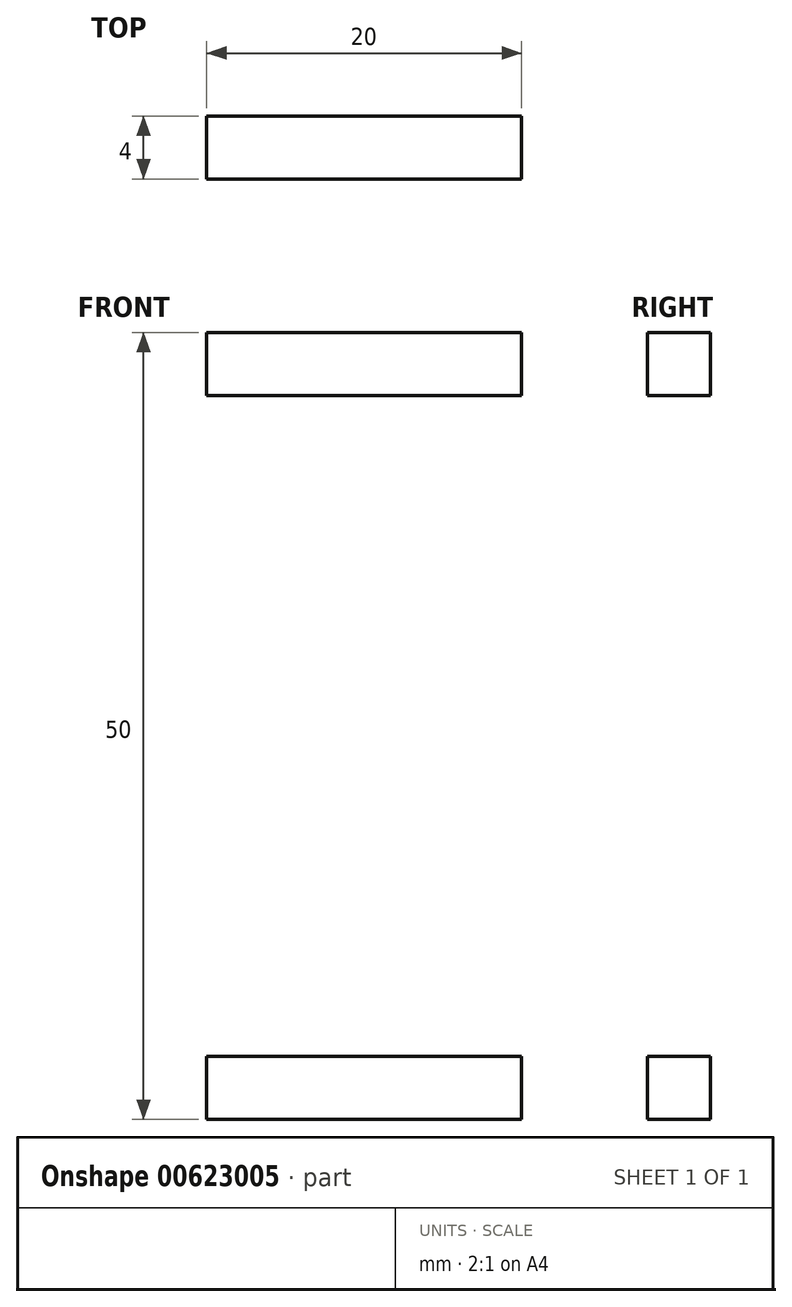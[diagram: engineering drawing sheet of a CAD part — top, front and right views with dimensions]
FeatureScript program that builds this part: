
annotation { "Feature Type Name" : "Feature", "Feature Type Description" : "" }
export const myFeature = defineFeature(function(context is Context, id is Id, definition is map)
    precondition{}
    {
        {
            var Q0;
            Q0=qCreatedBy(makeId("Front.planeOp"),FACE);
            var sketch = newSketch(context, id + "F0", { "sketchPlane" : qUnion([Q0])});
            skLineSegment(sketch, "E0.bottom", {"start": v(0, 0) * mm, "end": v(-300, 0) * mm});
            skLineSegment(sketch, "E0.top", {"start": v(0, 50) * mm, "end": v(-300, 50) * mm});
            skLineSegment(sketch, "E0.left", {"start": v(0, 0) * mm, "end": v(0, 50) * mm});
            skLineSegment(sketch, "E0.right", {"start": v(-300, 0) * mm, "end": v(-300, 50) * mm});
            skLineSegment(sketch, "E1.bottom", {"start": v(-300, 0) * mm, "end": v(-280, 0) * mm});
            skLineSegment(sketch, "E1.top", {"start": v(-300, 4) * mm, "end": v(-280, 4) * mm});
            skLineSegment(sketch, "E1.left", {"start": v(-300, 0) * mm, "end": v(-300, 4) * mm});
            skLineSegment(sketch, "E1.right", {"start": v(-280, 0) * mm, "end": v(-280, 4) * mm});
            skLineSegment(sketch, "E2.bottom", {"start": v(-260, 0) * mm, "end": v(-240, 0) * mm});
            skLineSegment(sketch, "E2.top", {"start": v(-260, 4) * mm, "end": v(-240, 4) * mm});
            skLineSegment(sketch, "E2.left", {"start": v(-260, 0) * mm, "end": v(-260, 4) * mm});
            skLineSegment(sketch, "E2.right", {"start": v(-240, 0) * mm, "end": v(-240, 4) * mm});
            skLineSegment(sketch, "E3.bottom", {"start": v(-220, 0) * mm, "end": v(-200, 0) * mm});
            skLineSegment(sketch, "E3.top", {"start": v(-220, 4) * mm, "end": v(-200, 4) * mm});
            skLineSegment(sketch, "E3.left", {"start": v(-220, 0) * mm, "end": v(-220, 4) * mm});
            skLineSegment(sketch, "E3.right", {"start": v(-200, 0) * mm, "end": v(-200, 4) * mm});
            skLineSegment(sketch, "E4.bottom", {"start": v(-180, 0) * mm, "end": v(-160, 0) * mm});
            skLineSegment(sketch, "E4.top", {"start": v(-180, 4) * mm, "end": v(-160, 4) * mm});
            skLineSegment(sketch, "E4.left", {"start": v(-180, 0) * mm, "end": v(-180, 4) * mm});
            skLineSegment(sketch, "E4.right", {"start": v(-160, 0) * mm, "end": v(-160, 4) * mm});
            skLineSegment(sketch, "E5.bottom", {"start": v(-140, 0) * mm, "end": v(-120, 0) * mm});
            skLineSegment(sketch, "E5.top", {"start": v(-140, 4) * mm, "end": v(-120, 4) * mm});
            skLineSegment(sketch, "E5.left", {"start": v(-140, 0) * mm, "end": v(-140, 4) * mm});
            skLineSegment(sketch, "E5.right", {"start": v(-120, 0) * mm, "end": v(-120, 4) * mm});
            skLineSegment(sketch, "E6.bottom", {"start": v(-100, 0) * mm, "end": v(-80, 0) * mm});
            skLineSegment(sketch, "E6.top", {"start": v(-100, 4) * mm, "end": v(-80, 4) * mm});
            skLineSegment(sketch, "E6.left", {"start": v(-100, 0) * mm, "end": v(-100, 4) * mm});
            skLineSegment(sketch, "E6.right", {"start": v(-80, 0) * mm, "end": v(-80, 4) * mm});
            skLineSegment(sketch, "E7.bottom", {"start": v(-60, 0) * mm, "end": v(-40, 0) * mm});
            skLineSegment(sketch, "E7.top", {"start": v(-60, 4) * mm, "end": v(-40, 4) * mm});
            skLineSegment(sketch, "E7.left", {"start": v(-60, 0) * mm, "end": v(-60, 4) * mm});
            skLineSegment(sketch, "E7.right", {"start": v(-40, 0) * mm, "end": v(-40, 4) * mm});
            skLineSegment(sketch, "E8.bottom", {"start": v(0, 0) * mm, "end": v(-20, 0) * mm});
            skLineSegment(sketch, "E8.top", {"start": v(0, 4) * mm, "end": v(-20, 4) * mm});
            skLineSegment(sketch, "E8.left", {"start": v(0, 0) * mm, "end": v(0, 4) * mm});
            skLineSegment(sketch, "E8.right", {"start": v(-20, 0) * mm, "end": v(-20, 4) * mm});
            skLineSegment(sketch, "E9.bottom", {"start": v(-300, 50) * mm, "end": v(-280, 50) * mm});
            skLineSegment(sketch, "E9.top", {"start": v(-300, 46) * mm, "end": v(-280, 46) * mm});
            skLineSegment(sketch, "E9.left", {"start": v(-300, 50) * mm, "end": v(-300, 46) * mm});
            skLineSegment(sketch, "E9.right", {"start": v(-280, 50) * mm, "end": v(-280, 46) * mm});
            skLineSegment(sketch, "E10.bottom", {"start": v(-260, 50) * mm, "end": v(-240, 50) * mm});
            skLineSegment(sketch, "E10.top", {"start": v(-260, 46) * mm, "end": v(-240, 46) * mm});
            skLineSegment(sketch, "E10.left", {"start": v(-260, 50) * mm, "end": v(-260, 46) * mm});
            skLineSegment(sketch, "E10.right", {"start": v(-240, 50) * mm, "end": v(-240, 46) * mm});
            skLineSegment(sketch, "E11.bottom", {"start": v(-220, 50) * mm, "end": v(-200, 50) * mm});
            skLineSegment(sketch, "E11.top", {"start": v(-220, 46) * mm, "end": v(-200, 46) * mm});
            skLineSegment(sketch, "E11.left", {"start": v(-220, 50) * mm, "end": v(-220, 46) * mm});
            skLineSegment(sketch, "E11.right", {"start": v(-200, 50) * mm, "end": v(-200, 46) * mm});
            skLineSegment(sketch, "E12.bottom", {"start": v(-180, 50) * mm, "end": v(-160, 50) * mm});
            skLineSegment(sketch, "E12.top", {"start": v(-180, 46) * mm, "end": v(-160, 46) * mm});
            skLineSegment(sketch, "E12.left", {"start": v(-180, 50) * mm, "end": v(-180, 46) * mm});
            skLineSegment(sketch, "E12.right", {"start": v(-160, 50) * mm, "end": v(-160, 46) * mm});
            skLineSegment(sketch, "E13.bottom", {"start": v(-140, 50) * mm, "end": v(-120, 50) * mm});
            skLineSegment(sketch, "E13.top", {"start": v(-140, 46) * mm, "end": v(-120, 46) * mm});
            skLineSegment(sketch, "E13.left", {"start": v(-140, 50) * mm, "end": v(-140, 46) * mm});
            skLineSegment(sketch, "E13.right", {"start": v(-120, 50) * mm, "end": v(-120, 46) * mm});
            skLineSegment(sketch, "E14.bottom", {"start": v(-100, 50) * mm, "end": v(-80, 50) * mm});
            skLineSegment(sketch, "E14.top", {"start": v(-100, 46) * mm, "end": v(-80, 46) * mm});
            skLineSegment(sketch, "E14.left", {"start": v(-100, 50) * mm, "end": v(-100, 46) * mm});
            skLineSegment(sketch, "E14.right", {"start": v(-80, 50) * mm, "end": v(-80, 46) * mm});
            skLineSegment(sketch, "E15.bottom", {"start": v(-60, 50) * mm, "end": v(-40, 50) * mm});
            skLineSegment(sketch, "E15.top", {"start": v(-60, 46) * mm, "end": v(-40, 46) * mm});
            skLineSegment(sketch, "E15.left", {"start": v(-60, 50) * mm, "end": v(-60, 46) * mm});
            skLineSegment(sketch, "E15.right", {"start": v(-40, 50) * mm, "end": v(-40, 46) * mm});
            skLineSegment(sketch, "E16.bottom", {"start": v(-20, 50) * mm, "end": v(0, 50) * mm});
            skLineSegment(sketch, "E16.top", {"start": v(-20, 46) * mm, "end": v(0, 46) * mm});
            skLineSegment(sketch, "E16.left", {"start": v(-20, 50) * mm, "end": v(-20, 46) * mm});
            skLineSegment(sketch, "E16.right", {"start": v(0, 50) * mm, "end": v(0, 46) * mm});
            skSolve(sketch);
        }
        {
            var Q0;
            Q0=makeQuery(id+"F0.imprint","IMPRINT",FACE,{"disambiguationData":[TD([[makeQuery(id+"F0.imprint","IMPRINT",EDGE,{"derivedFrom":sQuery(id+"F0.wireOp",EDGE,"E0.left")}),1.0]])]});
            extrude(context, id + "F1", {"entities" : qUnion([Q0]), "depth" : 4 * mm, "offsetDistance" : 25 * mm});
        }
        {
            var Q0;
            Q0=qCreatedBy(makeId("Front.planeOp"),FACE);
            var sketch = newSketch(context, id + "F2", { "sketchPlane" : qUnion([Q0])});
            skLineSegment(sketch, "E17.bottom", {"start": v(0, 46) * mm, "end": v(-4, 46) * mm});
            skLineSegment(sketch, "E17.top", {"start": v(0, 32) * mm, "end": v(-4, 32) * mm});
            skLineSegment(sketch, "E17.left", {"start": v(0, 46) * mm, "end": v(0, 32) * mm});
            skLineSegment(sketch, "E17.right", {"start": v(-4, 46) * mm, "end": v(-4, 32) * mm});
            skLineSegment(sketch, "E18.bottom", {"start": v(0, 4) * mm, "end": v(-4, 4) * mm});
            skLineSegment(sketch, "E18.top", {"start": v(0, 18) * mm, "end": v(-4, 18) * mm});
            skLineSegment(sketch, "E18.left", {"start": v(0, 4) * mm, "end": v(0, 18) * mm});
            skLineSegment(sketch, "E18.right", {"start": v(-4, 4) * mm, "end": v(-4, 18) * mm});
            skLineSegment(sketch, "E19.bottom", {"start": v(-300, 4) * mm, "end": v(-296, 4) * mm});
            skLineSegment(sketch, "E19.top", {"start": v(-300, 18) * mm, "end": v(-296, 18) * mm});
            skLineSegment(sketch, "E19.left", {"start": v(-300, 4) * mm, "end": v(-300, 18) * mm});
            skLineSegment(sketch, "E19.right", {"start": v(-296, 4) * mm, "end": v(-296, 18) * mm});
            skLineSegment(sketch, "E20.bottom", {"start": v(-300, 46) * mm, "end": v(-296, 46) * mm});
            skLineSegment(sketch, "E20.top", {"start": v(-300, 32) * mm, "end": v(-296, 32) * mm});
            skLineSegment(sketch, "E20.left", {"start": v(-300, 32) * mm, "end": v(-300, 46) * mm});
            skLineSegment(sketch, "E20.right", {"start": v(-296, 32) * mm, "end": v(-296, 46) * mm});
            skSolve(sketch);
        }
        {
            var Q0;
            Q0 = qSketchRegion(id + "F2", true);
            extrude(context, id + "F3", {"entities" : qUnion([Q0]), "operationType" : NewBodyOperationType.REMOVE, "depth" : 4 * mm, "offsetDistance" : 25 * mm});
        }
    });
